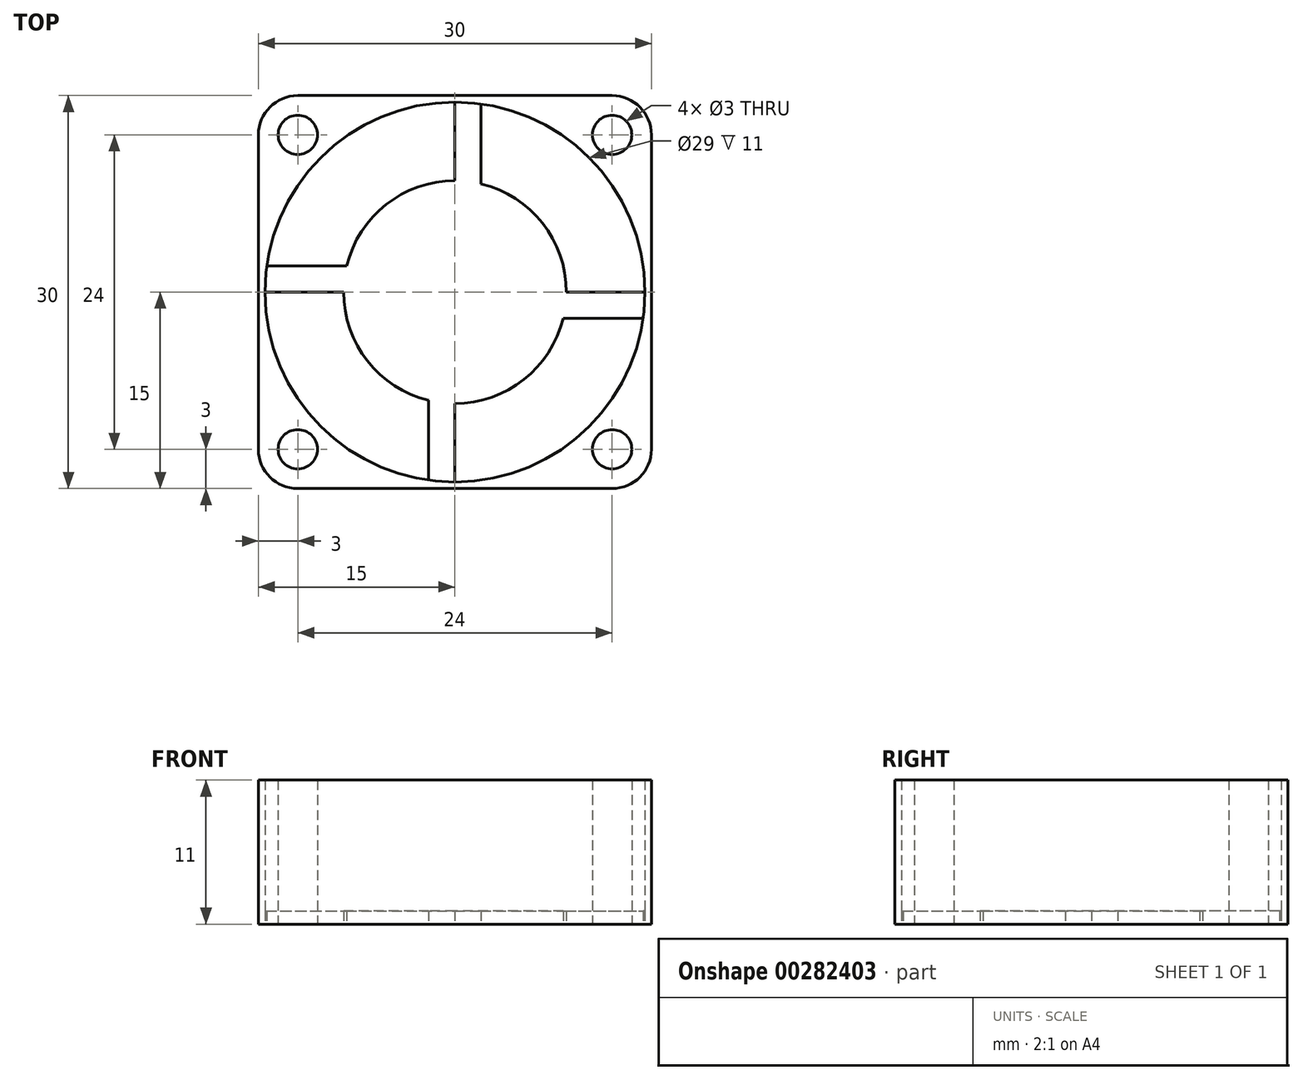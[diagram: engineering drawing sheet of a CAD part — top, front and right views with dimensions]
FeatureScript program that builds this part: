
annotation { "Feature Type Name" : "Feature", "Feature Type Description" : "" }
export const myFeature = defineFeature(function(context is Context, id is Id, definition is map)
    precondition{}
    {
        {
            var Q0;
            Q0=qCreatedBy(makeId("Top.planeOp"),FACE);
            var sketch = newSketch(context, id + "F0", { "sketchPlane" : qUnion([Q0])});
            skLineSegment(sketch, "E0.bottom", {"start": v(12, -15) * mm, "end": v(-12, -15) * mm});
            skLineSegment(sketch, "E0.top", {"start": v(12, 15) * mm, "end": v(-12, 15) * mm});
            skLineSegment(sketch, "E0.left", {"start": v(15, -12) * mm, "end": v(15, 12) * mm});
            skLineSegment(sketch, "E0.right", {"start": v(-15, -12) * mm, "end": v(-15, 12) * mm});
            skPoint(sketch, "E0.middle", {"position": v(0, 0) * mm});
            skCircle(sketch, "E1", {"center": v(0, 0) * mm, "radius": 14.5 * mm});
            skCircle(sketch, "E2", {"center": v(-12, 12) * mm, "radius": 1.5 * mm});
            skPoint(sketch, "E3.visualSharp", {"position": v(-15, 15) * mm});
            skArc(sketch, "E3.filletArc", {"start": v(-12, 15) * mm, "mid": v(-14.12, 14.12) * mm, "end": v(-15, 12) * mm});
            skPoint(sketch, "E4.visualSharp", {"position": v(15, 15) * mm});
            skArc(sketch, "E4.filletArc", {"start": v(15, 12) * mm, "mid": v(14.12, 14.12) * mm, "end": v(12, 15) * mm});
            skPoint(sketch, "E5.visualSharp", {"position": v(15, -15) * mm});
            skArc(sketch, "E5.filletArc", {"start": v(12, -15) * mm, "mid": v(14.12, -14.12) * mm, "end": v(15, -12) * mm});
            skPoint(sketch, "E6.visualSharp", {"position": v(-15, -15) * mm});
            skArc(sketch, "E6.filletArc", {"start": v(-15, -12) * mm, "mid": v(-14.12, -14.12) * mm, "end": v(-12, -15) * mm});
            skCircle(sketch, "E7", {"center": v(12, 12) * mm, "radius": 1.5 * mm});
            skCircle(sketch, "E8", {"center": v(12, -12) * mm, "radius": 1.5 * mm});
            skCircle(sketch, "E9", {"center": v(-12, -12) * mm, "radius": 1.5 * mm});
            skSolve(sketch);
        }
        {
            var Q0;
            Q0=qSketchRegion(id+"F0",true);
            extrude(context, id + "F1", {"entities" : qUnion([Q0]), "depth" : 11 * mm});
        }
        {
            var Q0;
            Q0=makeQuery(id+"F1.opExtrude","CAP_FACE",FACE,{"disambiguationData":[OSD([sQuery(id+"F0.wireOp",EDGE,"E0.bottom"),sQuery(id+"F0.wireOp",EDGE,"E0.top"),sQuery(id+"F0.wireOp",EDGE,"E0.left"),sQuery(id+"F0.wireOp",EDGE,"E0.right"),sQuery(id+"F0.wireOp",EDGE,"E1"),sQuery(id+"F0.wireOp",EDGE,"E2"),sQuery(id+"F0.wireOp",EDGE,"E3.filletArc"),sQuery(id+"F0.wireOp",EDGE,"E4.filletArc"),sQuery(id+"F0.wireOp",EDGE,"E5.filletArc"),sQuery(id+"F0.wireOp",EDGE,"E6.filletArc"),sQuery(id+"F0.wireOp",EDGE,"E7"),sQuery(id+"F0.wireOp",EDGE,"E8"),sQuery(id+"F0.wireOp",EDGE,"E9")])],"isStart":true});
            var sketch = newSketch(context, id + "F2", { "sketchPlane" : qUnion([Q0])});
            skArc(sketch, "E10", {"start": v(2, -8.26) * mm, "mid": v(6.68, -5.26) * mm, "end": v(8.5, 0) * mm});
            skLineSegment(sketch, "E11", {"start": v(8.5, 0) * mm, "end": v(15, 0) * mm});
            skLineSegment(sketch, "E12", {"start": v(0, 15) * mm, "end": v(0, 8.5) * mm});
            skLineSegment(sketch, "E13", {"start": v(-15, 0) * mm, "end": v(-8.5, 0) * mm});
            skLineSegment(sketch, "E14", {"start": v(0, -15) * mm, "end": v(0, -8.5) * mm});
            skLineSegment(sketch, "E15.0", {"start": v(2, -15) * mm, "end": v(2, -8.26) * mm});
            skLineSegment(sketch, "E16.0", {"start": v(8.26, 2) * mm, "end": v(15, 2) * mm});
            skLineSegment(sketch, "E17.0", {"start": v(-2, 15) * mm, "end": v(-2, 8.26) * mm});
            skLineSegment(sketch, "E18.0", {"start": v(-15, -2) * mm, "end": v(-8.26, -2) * mm});
            skLineSegment(sketch, "E19", {"start": v(-15, 0) * mm, "end": v(-15, -2) * mm});
            skLineSegment(sketch, "E20", {"start": v(0, -15) * mm, "end": v(2, -15) * mm});
            skLineSegment(sketch, "E21", {"start": v(15, 0) * mm, "end": v(15, 2) * mm});
            skLineSegment(sketch, "E22", {"start": v(0, 15) * mm, "end": v(-2, 15) * mm});
            skLineSegment(sketch, "E23.trimOffspring", {"start": v(0, -2) * mm, "end": v(0, 0) * mm});
            skArc(sketch, "E24.trimOffspring", {"start": v(8.26, 2) * mm, "mid": v(5.26, 6.68) * mm, "end": v(0, 8.5) * mm});
            skArc(sketch, "E25.trimOffspring", {"start": v(-2, 8.26) * mm, "mid": v(-6.68, 5.26) * mm, "end": v(-8.5, 0) * mm});
            skArc(sketch, "E26.trimOffspring", {"start": v(-8.26, -2) * mm, "mid": v(-5.26, -6.68) * mm, "end": v(0, -8.5) * mm});
            skSolve(sketch);
        }
        {
            var Q0;
            Q0=qSketchRegion(id+"F2",true);
            extrude(context, id + "F3", {"entities" : qUnion([Q0]), "operationType" : NewBodyOperationType.ADD, "oppositeDirection" : true, "depth" : 1 * mm});
        }
    });
